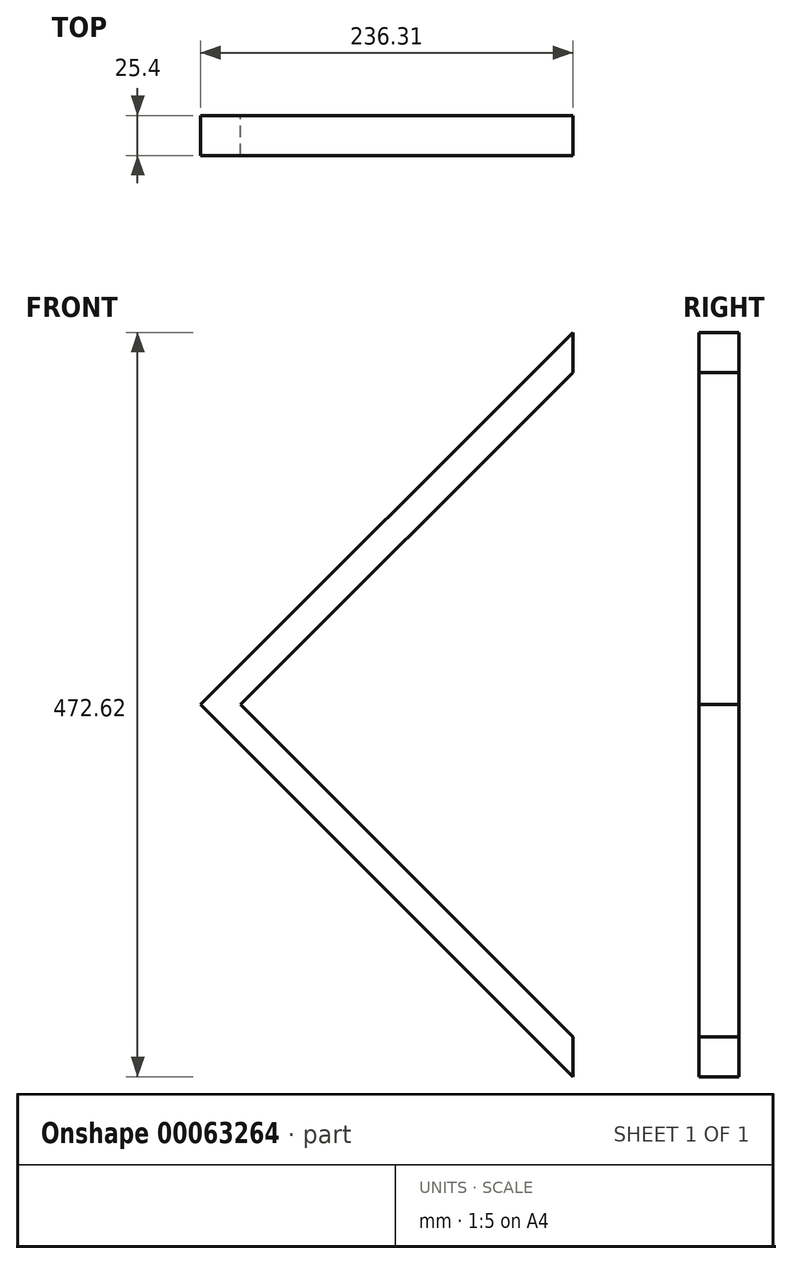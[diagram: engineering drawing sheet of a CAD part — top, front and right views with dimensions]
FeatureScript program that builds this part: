
annotation { "Feature Type Name" : "Feature", "Feature Type Description" : "" }
export const myFeature = defineFeature(function(context is Context, id is Id, definition is map)
    precondition{}
    {
        {
            var Q0;
            Q0=qCreatedBy(makeId("Front.planeOp"),FACE);
            var sketch = newSketch(context, id + "F0", { "sketchPlane" : qUnion([Q0])});
            skLineSegment(sketch, "E0", {"start": v(0, 236.3) * mm, "end": v(-236.3, 0) * mm});
            skLineSegment(sketch, "E1", {"start": v(-236.3, 0) * mm, "end": v(0, -236.3) * mm});
            skLineSegment(sketch, "E2", {"start": v(0, -236.3) * mm, "end": v(0, -210.9) * mm});
            skLineSegment(sketch, "E3", {"start": v(0, -210.9) * mm, "end": v(0, -210.9) * mm});
            skLineSegment(sketch, "E4", {"start": v(0, -210.9) * mm, "end": v(-210.9, 0) * mm});
            skLineSegment(sketch, "E5", {"start": v(0, 236.3) * mm, "end": v(0, 210.9) * mm});
            skLineSegment(sketch, "E6", {"start": v(0, 210.9) * mm, "end": v(0, 210.9) * mm});
            skLineSegment(sketch, "E7", {"start": v(0, 210.9) * mm, "end": v(-210.9, 0) * mm});
            skSolve(sketch);
        }
        {
            var Q0;
            Q0=makeQuery(id+"F0.imprint","IMPRINT",FACE,{"disambiguationData":[TD([[makeQuery(id+"F0.imprint","IMPRINT",EDGE,{"derivedFrom":sQuery(id+"F0.wireOp",EDGE,"E0")}),1.0]])]});
            extrude(context, id + "F1", {"entities" : qUnion([Q0]), "depth" : 25.4 * mm});
        }
    });
